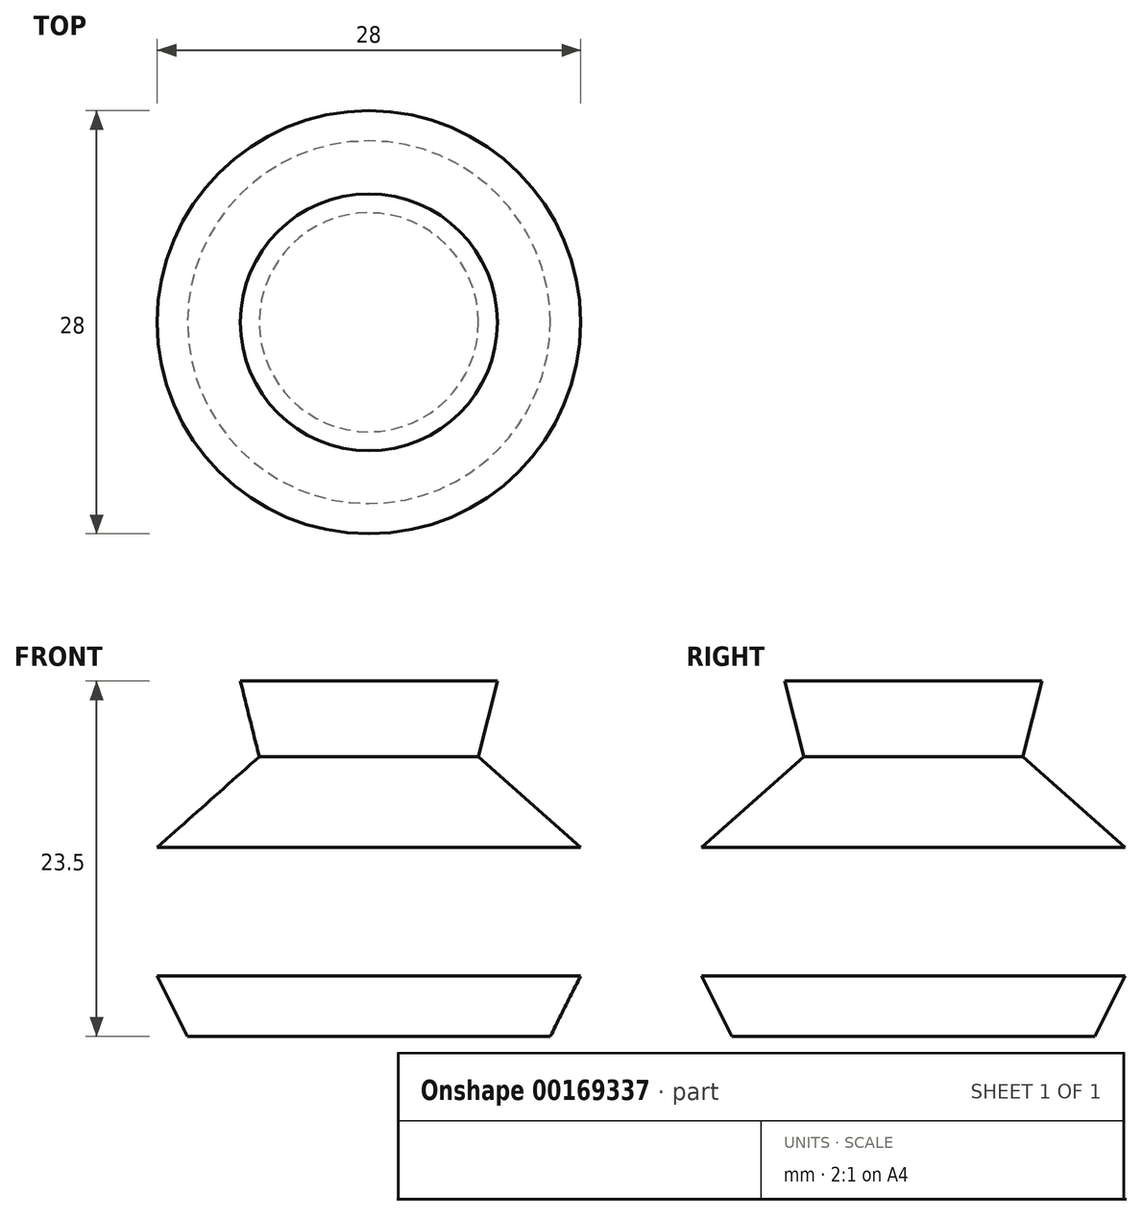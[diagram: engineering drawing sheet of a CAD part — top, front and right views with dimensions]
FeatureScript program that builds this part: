
annotation { "Feature Type Name" : "Feature", "Feature Type Description" : "" }
export const myFeature = defineFeature(function(context is Context, id is Id, definition is map)
    precondition{}
    {
        {
            var Q0;
            Q0=qCreatedBy(makeId("Front.planeOp"),FACE);
            var sketch = newSketch(context, id + "F0", { "sketchPlane" : qUnion([Q0])});
            skLineSegment(sketch, "E0", {"start": v(0, 0) * mm, "end": v(12, 0) * mm});
            skLineSegment(sketch, "E1", {"start": v(12, 0) * mm, "end": v(14, 4) * mm});
            skLineSegment(sketch, "E2", {"start": v(14, 4) * mm, "end": v(0, 4) * mm});
            skLineSegment(sketch, "E3", {"start": v(0, 4) * mm, "end": v(0, 0) * mm});
            skLineSegment(sketch, "E4.bottom", {"start": v(0, 4) * mm, "end": v(14, 4) * mm});
            skLineSegment(sketch, "E4.top", {"start": v(0, 12.5) * mm, "end": v(14, 12.5) * mm});
            skLineSegment(sketch, "E4.left", {"start": v(0, 4) * mm, "end": v(0, 12.5) * mm});
            skLineSegment(sketch, "E4.right", {"start": v(14, 4) * mm, "end": v(14, 12.5) * mm});
            skLineSegment(sketch, "E5", {"start": v(0, 12.5) * mm, "end": v(0, 18.5) * mm});
            skLineSegment(sketch, "E6", {"start": v(0, 18.5) * mm, "end": v(7.25, 18.5) * mm});
            skLineSegment(sketch, "E7", {"start": v(7.25, 18.5) * mm, "end": v(14, 12.5) * mm});
            skLineSegment(sketch, "E8", {"start": v(0, 18.5) * mm, "end": v(0, 23.5) * mm});
            skLineSegment(sketch, "E9", {"start": v(0, 23.5) * mm, "end": v(8.5, 23.5) * mm});
            skLineSegment(sketch, "E10", {"start": v(8.5, 23.5) * mm, "end": v(7.25, 18.5) * mm});
            skLineSegment(sketch, "E11.bottom", {"start": v(0, 23.5) * mm, "end": v(2.5, 23.5) * mm});
            skLineSegment(sketch, "E11.top", {"start": v(0, 41) * mm, "end": v(2.5, 41) * mm});
            skLineSegment(sketch, "E11.left", {"start": v(0, 23.5) * mm, "end": v(0, 41) * mm});
            skLineSegment(sketch, "E11.right", {"start": v(2.5, 23.5) * mm, "end": v(2.5, 41) * mm});
            skSolve(sketch);
        }
        {
            var Q0;
            Q0=makeQuery(id+"F0.imprint","IMPRINT",FACE,{"disambiguationData":[TD([[makeQuery(id+"F0.imprint","IMPRINT",EDGE,{"derivedFrom":sQuery(id+"F0.wireOp",EDGE,"E0")}),1.0]])]});
            var Q1;
            Q1=sQuery(id+"F0.wireOp",EDGE,"E3");
            revolve(context, id + "F1", {"entities" : qUnion([Q0]), "axis" : qUnion([Q1]), "revolveType" : RevolveType.FULL});
        }
        {
            var Q0;
            Q0=makeQuery(id+"F0.imprint","IMPRINT",FACE,{"disambiguationData":[TD([[makeQuery(id+"F0.imprint","IMPRINT",EDGE,{"derivedFrom":sQuery(id+"F0.wireOp",EDGE,"E4.bottom")}),1.0]])]});
            var Q1;
            Q1=makeQuery(id+"F0.imprint","IMPRINT",FACE,{"disambiguationData":[TD([[makeQuery(id+"F0.imprint","IMPRINT",EDGE,{"derivedFrom":sQuery(id+"F0.wireOp",EDGE,"E4.top")}),1.0]])]});
            var Q2;
            Q2=makeQuery(id+"F0.imprint","IMPRINT",FACE,{"disambiguationData":[TD([[makeQuery(id+"F0.imprint","IMPRINT",EDGE,{"derivedFrom":sQuery(id+"F0.wireOp",EDGE,"E6")}),1.0]])]});
            var Q3;
            Q3=makeQuery(id+"F0.imprint","IMPRINT",FACE,{"disambiguationData":[TD([[makeQuery(id+"F0.imprint","IMPRINT",EDGE,{"derivedFrom":sQuery(id+"F0.wireOp",EDGE,"E11.bottom")}),1.0]])]});
            var Q4;
            Q4=sQuery(id+"F0.wireOp",EDGE,"E11.left");
            revolve(context, id + "F2", {"entities" : qUnion([Q0, Q1, Q2, Q3]), "axis" : qUnion([Q4]), "revolveType" : RevolveType.FULL});
        }
    });
